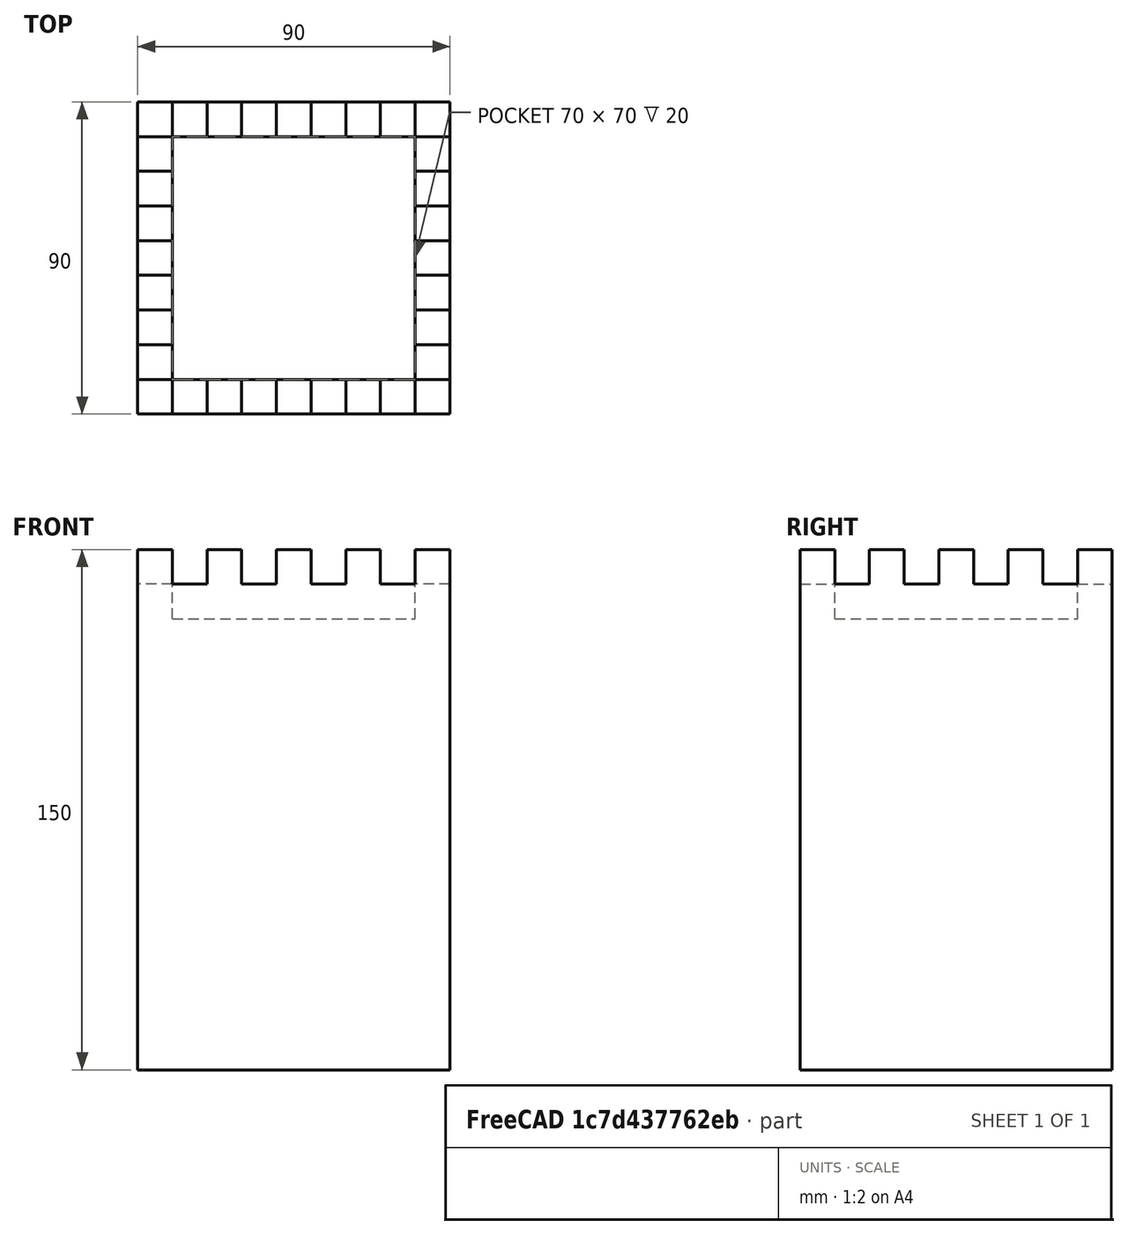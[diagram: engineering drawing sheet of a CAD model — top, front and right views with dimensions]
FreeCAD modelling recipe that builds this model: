
FCSTD DOCUMENT  (FreeCAD 0.18.4R)
Label: tutorial_freecad_ex10_c
License: All rights reserved
LicenseURL: http://en.wikipedia.org/wiki/All_rights_reserved
objects: Part::Box×4, Part::Cut×2, Part::FeaturePython×2, Part::Fuse×1
note: 9 computed .brp shape members not serialized (recipe doc carries the construction recipe); baked Part::Feature solids carry a one-line shape summary decoded from their .brp

FEATURE [Part::Box] Box  label="torre"
  AttacherType = Attacher::AttachEngine3D
  Height = 150
  Length = 90
  Width = 90
FEATURE [Part::Box] Box001  label="azotea_resta"
  AttacherType = Attacher::AttachEngine3D
  Height = 30
  Length = 70
  Placement = pos=(10,10,130) rot=(0,0,1;0rad)
  Width = 70
FEATURE [Part::Cut] Cut  label="torre_azotea"
  Base = -> Box
  Refine = true
  Tool = -> Box001
FEATURE [Part::Box] Box002  label="Cubo"
  AttacherType = Attacher::AttachEngine3D
  Height = 10
  Length = 10
  Width = 110
FEATURE [Part::FeaturePython] Array  label="almenas_x"  # Draft array (typed FeaturePython)
  Angle = 360
  ArrayType = 0
  Axis = (0,0,1)
  Base = -> Box002
  Center = (0,0,0)
  Fuse = false
  IntervalAxis = (0,0,0)
  IntervalX = (20,0,0)
  IntervalY = (0,1,0)
  IntervalZ = (0,0,1)
  NumberPolar = 1
  NumberX = 4
  NumberY = 1
  NumberZ = 1
FEATURE [Part::Box] Box003  label="Cubo001"
  AttacherType = Attacher::AttachEngine3D
  Height = 10
  Length = 10
  Width = 110
FEATURE [Part::FeaturePython] Array001  label="almenas_y"  # Draft array (typed FeaturePython)
  Angle = 360
  ArrayType = 0
  Axis = (0,0,1)
  Base = -> Box003
  Center = (0,0,0)
  Fuse = false
  IntervalAxis = (0,0,0)
  IntervalX = (20,0,0)
  IntervalY = (0,1,0)
  IntervalZ = (0,0,1)
  NumberPolar = 1
  NumberX = 4
  NumberY = 1
  NumberZ = 1
  Placement = pos=(90,20,0) rot=(0,0,1;1.5708rad)
FEATURE [Part::Fuse] Fusion  label="almena_resta"
  Base = -> Array
  Placement = pos=(10,-10,140) rot=(0,0,1;0rad)
  Refine = true
  Tool = -> Array001
FEATURE [Part::Cut] Cut001  label="torre_almenas"
  Base = -> Cut
  Refine = true
  Tool = -> Fusion
